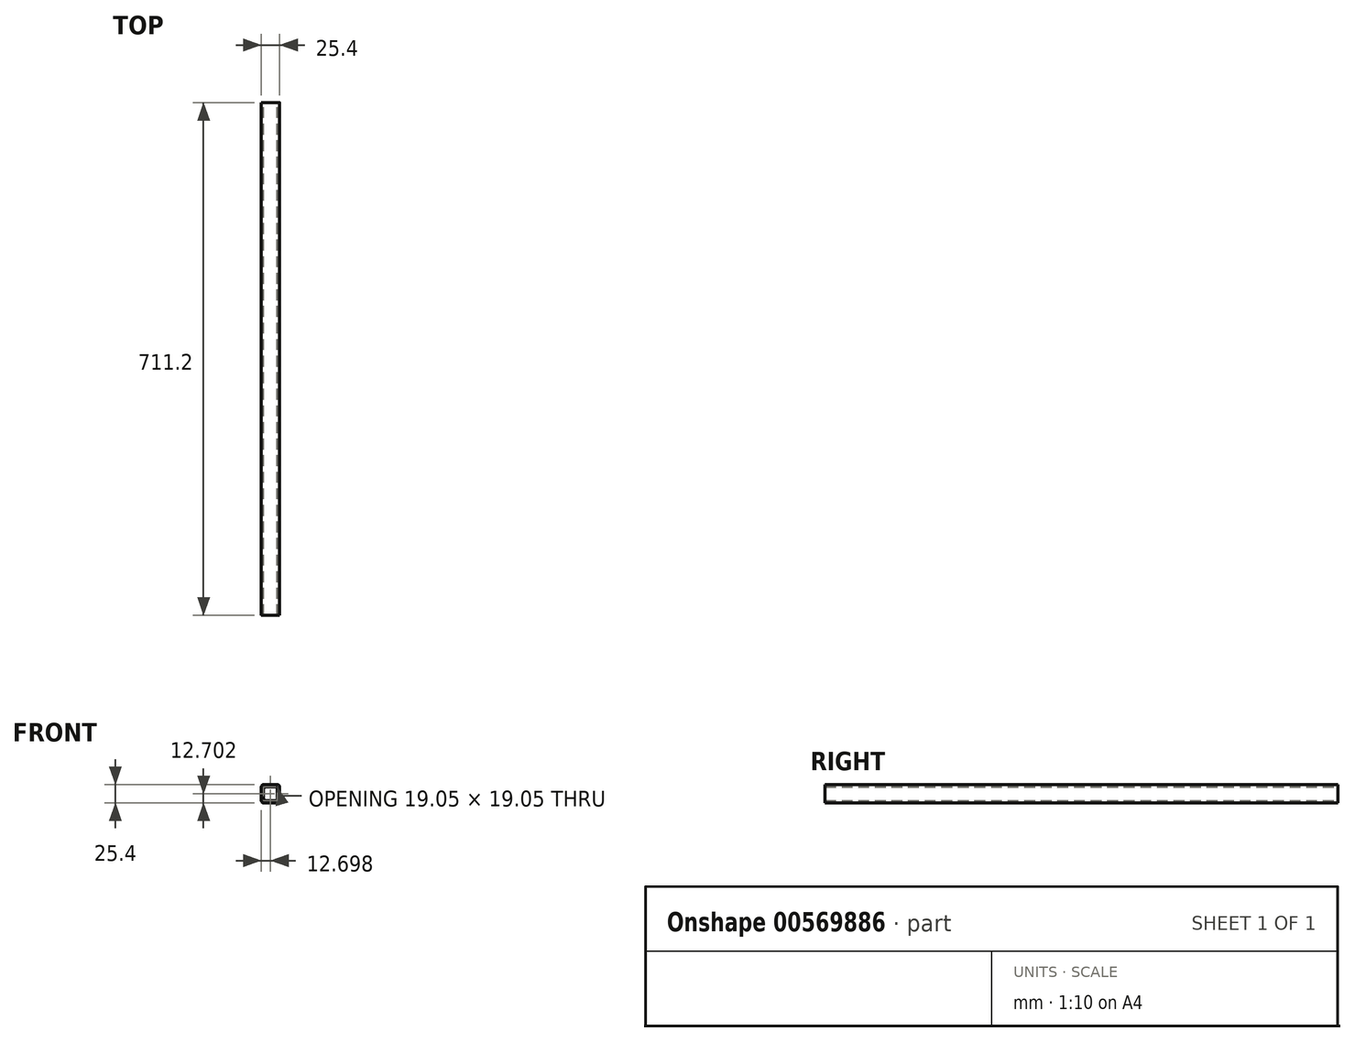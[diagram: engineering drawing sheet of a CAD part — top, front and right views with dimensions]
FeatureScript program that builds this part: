
annotation { "Feature Type Name" : "Feature", "Feature Type Description" : "" }
export const myFeature = defineFeature(function(context is Context, id is Id, definition is map)
    precondition{}
    {
        {
            var Q0;
            Q0=qCreatedBy(makeId("Front.planeOp"),FACE);
            var sketch = newSketch(context, id + "F0", { "sketchPlane" : qUnion([Q0])});
            skLineSegment(sketch, "E0.bottom", {"start": v(8.82, -13.08) * mm, "end": v(-10.23, -13.08) * mm});
            skLineSegment(sketch, "E0.top", {"start": v(8.82, 12.32) * mm, "end": v(-10.23, 12.32) * mm});
            skLineSegment(sketch, "E0.left", {"start": v(12, -9.9) * mm, "end": v(12, 9.15) * mm});
            skLineSegment(sketch, "E0.right", {"start": v(-13.4, -9.9) * mm, "end": v(-13.4, 9.15) * mm});
            skLineSegment(sketch, "E1.bottom", {"start": v(5.65, -9.9) * mm, "end": v(-7.05, -9.9) * mm});
            skLineSegment(sketch, "E1.top", {"start": v(5.65, 9.15) * mm, "end": v(-7.05, 9.15) * mm});
            skLineSegment(sketch, "E1.left", {"start": v(8.82, -6.73) * mm, "end": v(8.82, 5.97) * mm});
            skLineSegment(sketch, "E1.right", {"start": v(-10.23, -6.73) * mm, "end": v(-10.23, 5.97) * mm});
            skPoint(sketch, "E2.visualSharp", {"position": v(8.82, 9.15) * mm});
            skArc(sketch, "E2.filletArc", {"start": v(8.82, 5.97) * mm, "mid": v(7.9, 8.22) * mm, "end": v(5.65, 9.15) * mm});
            skPoint(sketch, "E3.visualSharp", {"position": v(-10.23, 9.15) * mm});
            skArc(sketch, "E3.filletArc", {"start": v(-7.05, 9.15) * mm, "mid": v(-9.3, 8.22) * mm, "end": v(-10.23, 5.97) * mm});
            skPoint(sketch, "E4.visualSharp", {"position": v(-10.23, -9.9) * mm});
            skArc(sketch, "E4.filletArc", {"start": v(-10.23, -6.73) * mm, "mid": v(-9.3, -8.97) * mm, "end": v(-7.05, -9.9) * mm});
            skPoint(sketch, "E5.visualSharp", {"position": v(8.82, -9.9) * mm});
            skArc(sketch, "E5.filletArc", {"start": v(5.65, -9.9) * mm, "mid": v(7.9, -8.97) * mm, "end": v(8.82, -6.73) * mm});
            skPoint(sketch, "E6.visualSharp", {"position": v(12, 12.32) * mm});
            skArc(sketch, "E6.filletArc", {"start": v(12, 9.15) * mm, "mid": v(11.07, 11.4) * mm, "end": v(8.82, 12.32) * mm});
            skPoint(sketch, "E7.visualSharp", {"position": v(-13.4, 12.32) * mm});
            skArc(sketch, "E7.filletArc", {"start": v(-10.23, 12.32) * mm, "mid": v(-12.47, 11.4) * mm, "end": v(-13.4, 9.15) * mm});
            skPoint(sketch, "E8.visualSharp", {"position": v(-13.4, -13.08) * mm});
            skArc(sketch, "E8.filletArc", {"start": v(-13.4, -9.9) * mm, "mid": v(-12.47, -12.15) * mm, "end": v(-10.23, -13.08) * mm});
            skPoint(sketch, "E9.visualSharp", {"position": v(12, -13.08) * mm});
            skArc(sketch, "E9.filletArc", {"start": v(8.82, -13.08) * mm, "mid": v(11.07, -12.15) * mm, "end": v(12, -9.9) * mm});
            skSolve(sketch);
        }
        {
            var Q0;
            Q0 = qSketchRegion(id + "F0", true);
            extrude(context, id + "F1", {"entities" : qUnion([Q0]), "depth" : 711.2 * mm, "offsetDistance" : 25.4 * mm});
        }
    });
